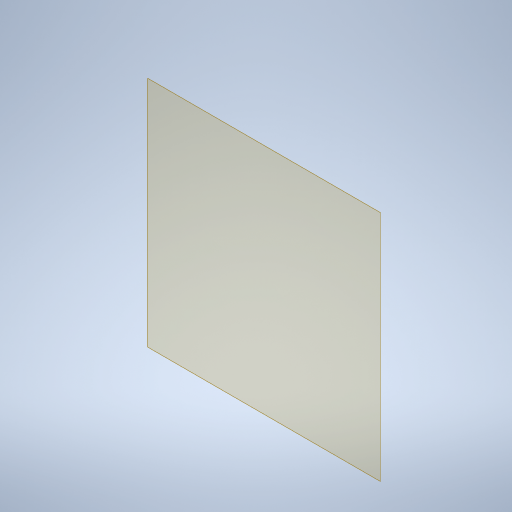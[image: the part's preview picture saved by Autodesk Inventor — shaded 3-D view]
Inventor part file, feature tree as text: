
AUTODESK INVENTOR PART (.ipt)
format: ipt  version: 2024 (Build 280153000, 153)  size: 623,616 bytes
history: native  units: mm
features: other x3, reference x2, plane x1, extrude x1, sketch x1
ambient origin geometry x8: Origin, YZ Plane, XZ Plane, XY Plane, X Axis, Y Axis, Z Axis, Center Point
bodies: Solid1 (feature_tree)
feature tree (8):
  plane  "Work Plane1"
  extrude  "Extrusion1"  Depth=4.0mm
  sketch  "Sketch1"  dims[d0=0.3mm d1=4.0mm d2=2.0mm d3=0.0mm]
  reference  "Reference1"
  reference  "Reference2"
  other  "<userpath>\Documents\Inventor\robot arm\arms\arms.iam"
  other  "arms.iam"
  other  "axle:1"
